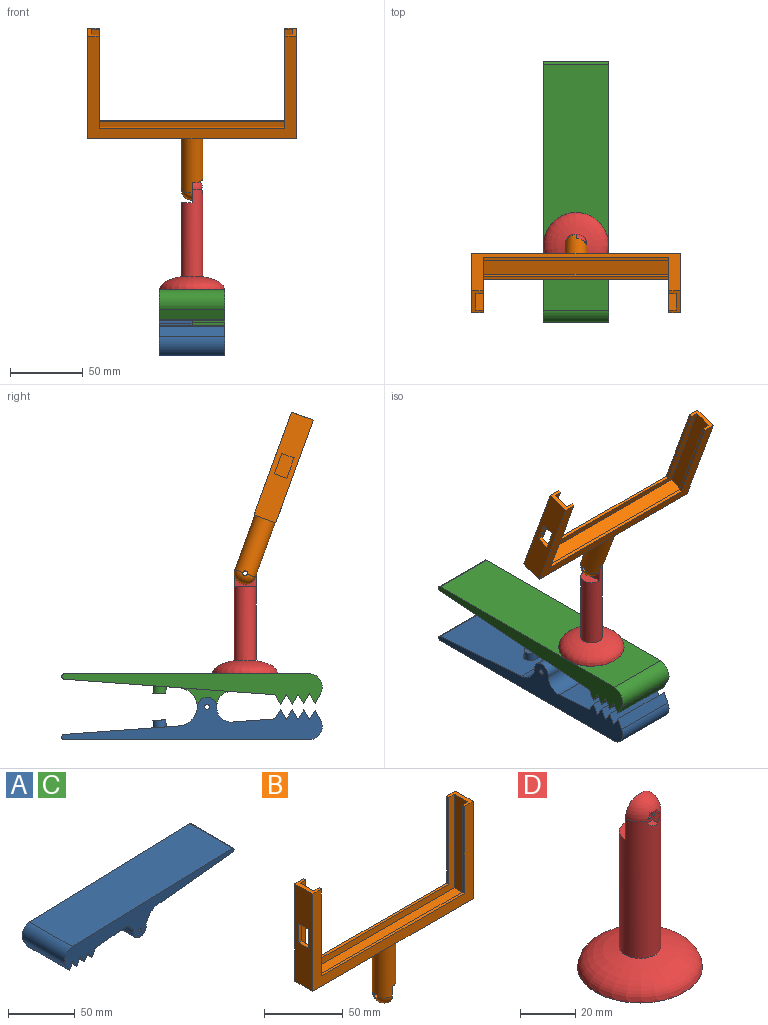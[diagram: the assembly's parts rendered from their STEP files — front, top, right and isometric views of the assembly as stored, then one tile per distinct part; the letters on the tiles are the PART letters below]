
ASSEMBLY  parts=4 mates=3
PART A: 23 faces, bbox 179.4x45x32.5 mm
  f0: plane 144.75x45mm, normal (0.1,0,-0.99), area 5622.7mm2, adj f9,f10,f12,f13,f14,f15,f17,f20
  f1: cylinder r=9.16mm len=45mm, axis (0,1,0), area 812.9mm2, adj f2,f11,f12,f13
  f2: plane 45x6.87mm, normal (-0.87,0,-0.5), area 356.9mm2, adj f1,f3,f12,f13
  f3: plane 45x6.87mm, normal (0.87,0,-0.5), area 356.9mm2, adj f2,f4,f12,f13
  f4: plane 45x6.87mm, normal (-0.87,0,-0.5), area 356.9mm2, adj f3,f5,f12,f13
  f5: plane 45x6.87mm, normal (0.87,0,-0.5), area 356.9mm2, adj f4,f6,f12,f13
  f6: plane 45x6.87mm, normal (-0.87,0,-0.5), area 356.9mm2, adj f5,f7,f12,f13
  f7: plane 45x6.87mm, normal (0.87,0,-0.5), area 356.9mm2, adj f6,f8,f12,f13
  f8: plane 45x6.87mm, normal (-0.87,0,-0.5), area 356.9mm2, adj f7,f9,f12,f13
  f9: plane 45x6.87mm, normal (0.87,0,-0.5), area 356.9mm2, adj f0,f8,f12,f13
  f10: cylinder r=1.89mm len=45mm, axis (0,1,0), area 249.4mm2, adj f0,f11,f12,f13
  f11: plane 169.65x45mm, normal (-0.03,0,1), area 7638.1mm2, adj f1,f10,f12,f13
  f12: plane 179.39x32.51mm, normal (0,-1,0), area 2149.9mm2, adj f0,f1,f2,f3,f4,f5,f6,f7
  f13: plane 179.39x25.86mm, normal (0,1,0), area 1872.5mm2, adj f0,f1,f2,f3,f4,f5,f6,f7
  f14: cylinder r=13.89mm len=22.5mm, axis (0,1,0), area 458.1mm2, adj f0,f12,f15,f18
  f15: plane 36.78x20.46mm, normal (0,1,0), area 277.4mm2, adj f0,f14,f16,f17,f18
  f16: cylinder r=1.65mm len=22.5mm, axis (0,1,0), area 233.3mm2, adj f12,f15
  f17: cylinder r=10mm len=22.5mm, axis (0,1,0), area 376.9mm2, adj f0,f12,f15,f18
  f18: cylinder r=6.65mm len=22.5mm, axis (0,1,0), area 470.1mm2, adj f12,f14,f15,f17
  f19: cylinder r=4.5mm len=9.68mm, axis (0.1,0,-0.99), area 197.9mm2, adj f21,f22
  f20: cylinder r=5.5mm len=11.15mm, axis (0.1,0,-0.99), area 69.1mm2, adj f0,f21
  f21: plane 11x10.94mm, normal (0.1,0,-0.99), area 31.4mm2, adj f19,f20
  f22: plane 9x8.95mm, normal (0.1,0,-0.99), area 63.6mm2, adj f19
PART B: 27 faces, bbox 144x16x122.8 mm
  f0: plane 75.5x16mm, normal (-1,0,0), area 1073mm2, adj f6,f13,f19,f21,f22,f23,f24,f25
  f1: plane 72.5x12mm, normal (1,0,0), area 735mm2, adj f6,f11,f15,f17,f22,f23,f24,f25
  f2: cylinder r=7.5mm len=39.85mm, axis (0,0,1), area 1696.7mm2, adj f3,f4,f5,f13,f26
  f3: sphere r=7.5mm, area 172.4mm2, adj f2,f4,f26
  f4: plane 15x15mm, normal (1,0,0), area 192.3mm2, adj f2,f3,f5,f26
  f5: plane 15x7.5mm, normal (0,0,-1), area 88.4mm2, adj f2,f4
  f6: plane 16x8mm, normal (0,0,1), area 68mm2, adj f0,f1,f8,f9,f15,f17,f19,f21
  f7: plane 16x8mm, normal (0,0,1), area 68mm2, adj f14,f15,f16,f17,f18,f19,f20,f21
  f8: plane 67.5x2mm, normal (1,0,0), area 135mm2, adj f6,f12,f17,f19
  f9: plane 67.5x2mm, normal (1,0,0), area 135mm2, adj f6,f10,f15,f21
  f10: plane 128x2mm, normal (0,0,1), area 256mm2, adj f9,f14,f15,f21
  f11: plane 138x12mm, normal (0,0,1), area 1656mm2, adj f1,f15,f16,f17
  f12: plane 128x2mm, normal (0,0,1), area 256mm2, adj f8,f17,f18,f19
  f13: plane 144x16mm, normal (0,0,-1), area 2127.3mm2, adj f0,f2,f19,f20,f21
  f14: plane 67.5x2mm, normal (-1,0,0), area 135mm2, adj f7,f10,f15,f21
  f15: plane 138x72.5mm, normal (0,-1,0), area 1365mm2, adj f1,f6,f7,f9,f10,f11,f14,f16
  f16: plane 72.5x12mm, normal (-1,0,0), area 870mm2, adj f7,f11,f15,f17
  f17: plane 138x72.5mm, normal (0,1,0), area 1365mm2, adj f1,f6,f7,f8,f11,f12,f16,f18
  f18: plane 67.5x2mm, normal (-1,0,0), area 135mm2, adj f7,f12,f17,f19
  f19: plane 144x75.5mm, normal (0,-1,0), area 2232mm2, adj f0,f6,f7,f8,f12,f13,f18,f20
  f20: plane 75.5x16mm, normal (1,0,0), area 1208mm2, adj f7,f13,f19,f21
  f21: plane 144x75.5mm, normal (0,1,0), area 2232mm2, adj f0,f6,f7,f9,f10,f13,f14,f20
  f22: plane 9x3mm, normal (0,0,-1), area 27mm2, adj f0,f1,f23,f25
  f23: plane 15x3mm, normal (0,-1,0), area 45mm2, adj f0,f1,f22,f24
  f24: plane 9x3mm, normal (0,0,1), area 27mm2, adj f0,f1,f23,f25
  f25: plane 15x3mm, normal (0,1,0), area 45mm2, adj f0,f1,f22,f24
  f26: cylinder r=1.65mm len=7.5mm, axis (1,0,0), area 76.3mm2, adj f2,f3,f4
PART C: same geometry as A
PART D: 14 faces, bbox 45x45x76.8 mm
  f0: cylinder r=7.5mm len=60.25mm, axis (0,0,-1), area 2605mm2, adj f1,f4,f5,f6,f10,f11,f12
  f1: sphere r=7.5mm, area 161.5mm2, adj f0,f6,f7,f8,f9
  f2: cylinder r=1.65mm len=4.7mm, axis (0,1,0), area 48.7mm2, adj f6,f13
  f3: plane 45x45mm, normal (0,0,-1), area 1590.4mm2, adj f4
  f4: revolved ~45x45mm, area 1898.9mm2, adj f0,f3
  f5: plane 15x7.5mm, normal (0,0,1), area 88.4mm2, adj f0,f6
  f6: plane 16.81x15mm, normal (0,1,0), area 219.5mm2, adj f0,f1,f2,f5
  f7: plane 2.9x2.22mm, normal (-0.87,0,-0.5), area 7.2mm2, adj f1,f8,f11,f13
  f8: plane 3.35x2.22mm, normal (0,0,-1), area 7.2mm2, adj f1,f7,f9,f13
  f9: plane 2.9x2.22mm, normal (0.87,0,-0.5), area 7.2mm2, adj f1,f8,f12,f13
  f10: plane 3.35x2.8mm, normal (0,0,1), area 9.2mm2, adj f0,f11,f12,f13
  f11: plane 2.9x2.61mm, normal (-0.87,0,0.5), area 7.9mm2, adj f0,f7,f10,f13
  f12: plane 2.9x2.61mm, normal (0.87,0,0.5), area 7.9mm2, adj f0,f9,f10,f13
  f13: plane 6.7x5.8mm, normal (0,-1,0), area 20.6mm2, adj f2,f7,f8,f9,f10,f11,f12
PLACE A rot(axis=(-0.71,-0.71,-0.01),178.7deg) t=(0,26.26,22.78)mm
PLACE B rot(axis=(1,0,0),20deg) t=(0,0,114.87)mm
PLACE C rot(axis=(-0.02,0.02,1),90deg) t=(0,26.26,22.78)mm
PLACE D rot(axis=(0,0,1),90deg) t=(0,0,45.55)mm
MATE revolute D.f2 <-> B.f26  axis (1,0,0) through (0,0,114.87)mm
MATE fastened C.f11 <-> D.f0  axis (0,0,1) through (0,0,45.55)mm
MATE revolute A.f16 <-> C.f16  axis (1,0,0) through (0,26.26,22.78)mm
